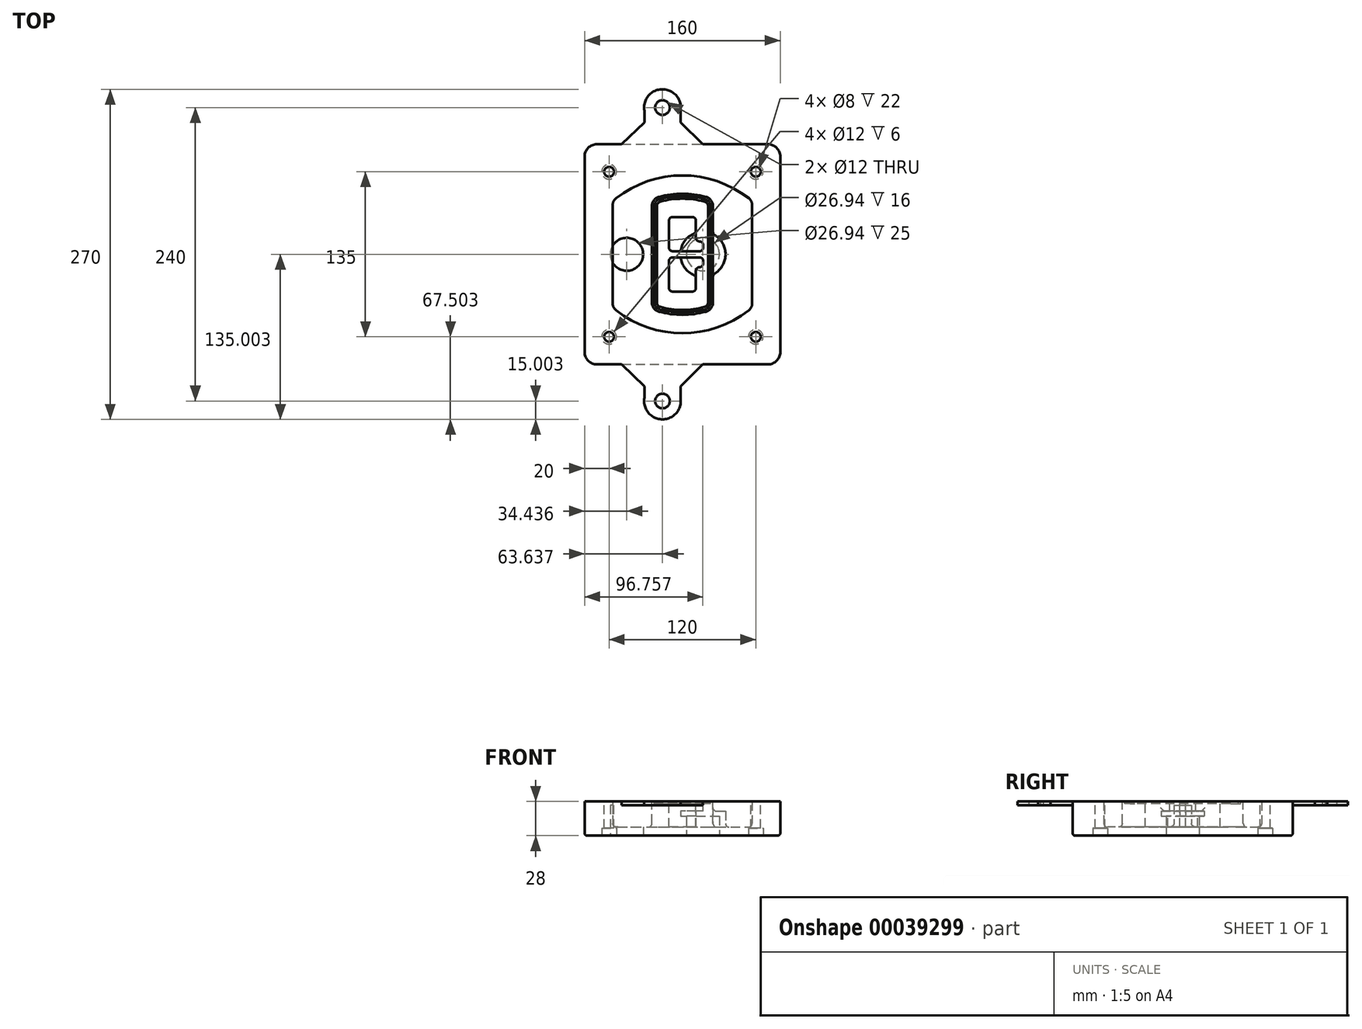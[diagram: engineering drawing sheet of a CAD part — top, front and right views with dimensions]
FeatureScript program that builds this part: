
annotation { "Feature Type Name" : "Feature", "Feature Type Description" : "" }
export const myFeature = defineFeature(function(context is Context, id is Id, definition is map)
    precondition{}
    {
        {
            var Q0;
            Q0=qCreatedBy(makeId("Top.planeOp"),FACE);
            var sketch = newSketch(context, id + "F0", { "sketchPlane" : qUnion([Q0])});
            skPoint(sketch, "E0.rect.middle", {"position": v(0, 0) * mm});
            skLineSegment(sketch, "E1.bottom", {"start": v(24.05, 28.38) * mm, "end": v(164.05, 28.38) * mm});
            skLineSegment(sketch, "E1.top", {"start": v(24.05, 208.38) * mm, "end": v(164.05, 208.38) * mm});
            skLineSegment(sketch, "E1.left", {"start": v(14.05, 38.38) * mm, "end": v(14.05, 198.38) * mm});
            skLineSegment(sketch, "E1.right", {"start": v(174.05, 38.38) * mm, "end": v(174.05, 198.38) * mm});
            skLineSegment(sketch, "E2", {"start": v(14.05, 208.38) * mm, "end": v(174.05, 28.38) * mm, "construction": true});
            skLineSegment(sketch, "E3", {"start": v(174.05, 208.38) * mm, "end": v(14.05, 28.38) * mm, "construction": true});
            skCircle(sketch, "E4", {"center": v(34.05, 185.88) * mm, "radius": 4 * mm});
            skCircle(sketch, "E5", {"center": v(154.05, 185.88) * mm, "radius": 4 * mm});
            skCircle(sketch, "E6", {"center": v(154.05, 50.88) * mm, "radius": 4 * mm});
            skCircle(sketch, "E7", {"center": v(34.05, 50.88) * mm, "radius": 4 * mm});
            skLineSegment(sketch, "E8", {"start": v(34.05, 185.88) * mm, "end": v(154.05, 185.88) * mm, "construction": true});
            skLineSegment(sketch, "E9", {"start": v(154.05, 185.88) * mm, "end": v(154.05, 50.88) * mm, "construction": true});
            skLineSegment(sketch, "E10", {"start": v(154.05, 50.88) * mm, "end": v(34.05, 50.88) * mm, "construction": true});
            skLineSegment(sketch, "E11", {"start": v(34.05, 50.88) * mm, "end": v(34.05, 185.88) * mm, "construction": true});
            skLineSegment(sketch, "E12", {"start": v(34.05, 158.68) * mm, "end": v(34.05, 78.09) * mm});
            skLineSegment(sketch, "E13", {"start": v(154.05, 158.68) * mm, "end": v(154.05, 78.09) * mm});
            skArc(sketch, "E14", {"start": v(150.2, 166.56) * mm, "mid": v(94.05, 185.88) * mm, "end": v(37.9, 166.56) * mm});
            skArc(sketch, "E15", {"start": v(37.9, 70.2) * mm, "mid": v(94.05, 50.88) * mm, "end": v(150.2, 70.2) * mm});
            skLineSegment(sketch, "E16", {"start": v(34.05, 118.38) * mm, "end": v(154.05, 118.38) * mm, "construction": true});
            skPoint(sketch, "E17.visualSharp", {"position": v(34.05, 73.38) * mm});
            skArc(sketch, "E17.filletArc", {"start": v(34.05, 78.09) * mm, "mid": v(35.06, 73.7) * mm, "end": v(37.9, 70.2) * mm});
            skPoint(sketch, "E18.visualSharp", {"position": v(34.05, 163.38) * mm});
            skArc(sketch, "E18.filletArc", {"start": v(37.9, 166.56) * mm, "mid": v(35.06, 163.06) * mm, "end": v(34.05, 158.68) * mm});
            skPoint(sketch, "E19.visualSharp", {"position": v(154.05, 163.38) * mm});
            skArc(sketch, "E19.filletArc", {"start": v(154.05, 158.68) * mm, "mid": v(153.04, 163.06) * mm, "end": v(150.2, 166.56) * mm});
            skPoint(sketch, "E20.visualSharp", {"position": v(154.05, 73.38) * mm});
            skArc(sketch, "E20.filletArc", {"start": v(150.2, 70.2) * mm, "mid": v(153.04, 73.7) * mm, "end": v(154.05, 78.09) * mm});
            skPoint(sketch, "E21.visualSharp", {"position": v(14.05, 208.38) * mm});
            skArc(sketch, "E21.filletArc", {"start": v(24.05, 208.38) * mm, "mid": v(16.98, 205.45) * mm, "end": v(14.05, 198.38) * mm});
            skPoint(sketch, "E22.visualSharp", {"position": v(174.05, 208.38) * mm});
            skArc(sketch, "E22.filletArc", {"start": v(174.05, 198.38) * mm, "mid": v(171.12, 205.45) * mm, "end": v(164.05, 208.38) * mm});
            skPoint(sketch, "E23.visualSharp", {"position": v(174.05, 28.38) * mm});
            skArc(sketch, "E23.filletArc", {"start": v(164.05, 28.38) * mm, "mid": v(171.12, 31.31) * mm, "end": v(174.05, 38.38) * mm});
            skPoint(sketch, "E24.visualSharp", {"position": v(14.05, 28.38) * mm});
            skArc(sketch, "E24.filletArc", {"start": v(14.05, 38.38) * mm, "mid": v(16.98, 31.31) * mm, "end": v(24.05, 28.38) * mm});
            skArc(sketch, "E25.0", {"start": v(151.05, 158.68) * mm, "mid": v(150.34, 161.75) * mm, "end": v(148.36, 164.2) * mm});
            skLineSegment(sketch, "E25.1", {"start": v(151.05, 158.68) * mm, "end": v(151.05, 78.09) * mm});
            skArc(sketch, "E25.2", {"start": v(148.36, 72.57) * mm, "mid": v(150.34, 75.02) * mm, "end": v(151.05, 78.09) * mm});
            skArc(sketch, "E25.3", {"start": v(39.74, 72.57) * mm, "mid": v(94.05, 53.88) * mm, "end": v(148.36, 72.57) * mm});
            skArc(sketch, "E25.4", {"start": v(37.05, 78.09) * mm, "mid": v(37.76, 75.02) * mm, "end": v(39.74, 72.57) * mm});
            skArc(sketch, "E25.5", {"start": v(148.36, 164.2) * mm, "mid": v(94.05, 182.88) * mm, "end": v(39.74, 164.2) * mm});
            skLineSegment(sketch, "E25.6", {"start": v(37.05, 158.68) * mm, "end": v(37.05, 78.09) * mm});
            skArc(sketch, "E25.7", {"start": v(39.74, 164.2) * mm, "mid": v(37.76, 161.75) * mm, "end": v(37.05, 158.68) * mm});
            skArc(sketch, "E26.0", {"start": v(35.43, 169.71) * mm, "mid": v(31.47, 164.82) * mm, "end": v(30.05, 158.68) * mm});
            skArc(sketch, "E26.1", {"start": v(152.67, 169.71) * mm, "mid": v(94.05, 189.88) * mm, "end": v(35.43, 169.71) * mm});
            skArc(sketch, "E26.2", {"start": v(158.05, 158.68) * mm, "mid": v(156.63, 164.82) * mm, "end": v(152.67, 169.71) * mm});
            skLineSegment(sketch, "E26.3", {"start": v(158.05, 158.68) * mm, "end": v(158.05, 78.09) * mm});
            skArc(sketch, "E26.4", {"start": v(152.67, 67.05) * mm, "mid": v(156.63, 71.95) * mm, "end": v(158.05, 78.09) * mm});
            skLineSegment(sketch, "E26.5", {"start": v(30.05, 158.68) * mm, "end": v(30.05, 78.09) * mm});
            skArc(sketch, "E26.6", {"start": v(35.43, 67.05) * mm, "mid": v(94.05, 46.88) * mm, "end": v(152.67, 67.05) * mm});
            skArc(sketch, "E26.7", {"start": v(30.05, 78.09) * mm, "mid": v(31.47, 71.95) * mm, "end": v(35.43, 67.05) * mm});
            skSolve(sketch);
        }
        {
            var Q0;
            Q0=makeQuery(id+"F0.imprint","IMPRINT",FACE,{"disambiguationData":[TD([[makeQuery(id+"F0.imprint","IMPRINT",EDGE,{"derivedFrom":sQuery(id+"F0.wireOp",EDGE,"E1.bottom")}),1.0]])]});
            var Q1;
            Q1=makeQuery(id+"F0.imprint","IMPRINT",FACE,{"disambiguationData":[TD([[makeQuery(id+"F0.imprint","IMPRINT",EDGE,{"derivedFrom":sQuery(id+"F0.wireOp",EDGE,"E12")}),1.0]])]});
            var Q2;
            Q2=makeQuery(id+"F0.imprint","IMPRINT",FACE,{"disambiguationData":[TD([[makeQuery(id+"F0.imprint","IMPRINT",EDGE,{"derivedFrom":sQuery(id+"F0.wireOp",EDGE,"E25.0")}),1.0]])]});
            var Q3;
            Q3=makeQuery(id+"F0.imprint","IMPRINT",FACE,{"disambiguationData":[TD([[makeQuery(id+"F0.imprint","IMPRINT",EDGE,{"derivedFrom":sQuery(id+"F0.wireOp",EDGE,"E12")}),-1.0]])]});
            extrude(context, id + "F1", {"entities" : qUnion([Q0, Q1, Q2, Q3]), "oppositeDirection" : true, "depth" : 25 * mm});
        }
        {
            var Q0;
            Q0=makeQuery(id+"F0.imprint","IMPRINT",FACE,{"disambiguationData":[TD([[makeQuery(id+"F0.imprint","IMPRINT",EDGE,{"derivedFrom":sQuery(id+"F0.wireOp",EDGE,"E12")}),1.0]])]});
            extrude(context, id + "F2", {"entities" : qUnion([Q0]), "operationType" : NewBodyOperationType.ADD, "depth" : 3 * mm});
        }
        {
            var Q0;
            Q0=makeQuery(id+"F0.imprint","IMPRINT",FACE,{"disambiguationData":[TD([[makeQuery(id+"F0.imprint","IMPRINT",EDGE,{"derivedFrom":sQuery(id+"F0.wireOp",EDGE,"E25.0")}),1.0]])]});
            extrude(context, id + "F3", {"entities" : qUnion([Q0]), "operationType" : NewBodyOperationType.REMOVE, "oppositeDirection" : true, "depth" : 18 * mm});
        }
        {
            var Q0;
            Q0=makeQuery(id+"F2.opExtrude","CAP_FACE",FACE,{"disambiguationData":[OSD([sQuery(id+"F0.wireOp",EDGE,"E12"),sQuery(id+"F0.wireOp",EDGE,"E13"),sQuery(id+"F0.wireOp",EDGE,"E14"),sQuery(id+"F0.wireOp",EDGE,"E15"),sQuery(id+"F0.wireOp",EDGE,"E17.filletArc"),sQuery(id+"F0.wireOp",EDGE,"E18.filletArc"),sQuery(id+"F0.wireOp",EDGE,"E19.filletArc"),sQuery(id+"F0.wireOp",EDGE,"E20.filletArc"),sQuery(id+"F0.wireOp",EDGE,"E25.0"),sQuery(id+"F0.wireOp",EDGE,"E25.1"),sQuery(id+"F0.wireOp",EDGE,"E25.2"),sQuery(id+"F0.wireOp",EDGE,"E25.3"),sQuery(id+"F0.wireOp",EDGE,"E25.4"),sQuery(id+"F0.wireOp",EDGE,"E25.5"),sQuery(id+"F0.wireOp",EDGE,"E25.6"),sQuery(id+"F0.wireOp",EDGE,"E25.7")])],"isStart":false});
            var sketch = newSketch(context, id + "F4", { "sketchPlane" : qUnion([Q0])});
            skArc(sketch, "E27.0", {"start": v(74.97, 71.41) * mm, "mid": v(94.05, 68.88) * mm, "end": v(113.13, 71.41) * mm});
            skArc(sketch, "E28.0", {"start": v(113.13, 165.35) * mm, "mid": v(94.05, 167.88) * mm, "end": v(74.97, 165.35) * mm});
            skLineSegment(sketch, "E29", {"start": v(69.05, 157.63) * mm, "end": v(69.05, 79.14) * mm});
            skLineSegment(sketch, "E30", {"start": v(119.05, 157.63) * mm, "end": v(119.05, 79.14) * mm});
            skLineSegment(sketch, "E31", {"start": v(69.05, 163.48) * mm, "end": v(119.05, 163.48) * mm, "construction": true});
            skLineSegment(sketch, "E32", {"start": v(69.05, 73.28) * mm, "end": v(119.05, 73.28) * mm, "construction": true});
            skPoint(sketch, "E33.visualSharp", {"position": v(69.05, 163.48) * mm});
            skArc(sketch, "E33.filletArc", {"start": v(74.97, 165.35) * mm, "mid": v(70.7, 162.5) * mm, "end": v(69.05, 157.63) * mm});
            skPoint(sketch, "E34.visualSharp", {"position": v(119.05, 163.48) * mm});
            skArc(sketch, "E34.filletArc", {"start": v(119.05, 157.63) * mm, "mid": v(117.4, 162.5) * mm, "end": v(113.13, 165.35) * mm});
            skPoint(sketch, "E35.visualSharp", {"position": v(119.05, 73.28) * mm});
            skArc(sketch, "E35.filletArc", {"start": v(113.13, 71.41) * mm, "mid": v(117.4, 74.27) * mm, "end": v(119.05, 79.14) * mm});
            skPoint(sketch, "E36.visualSharp", {"position": v(69.05, 73.28) * mm});
            skArc(sketch, "E36.filletArc", {"start": v(69.05, 79.14) * mm, "mid": v(70.7, 74.27) * mm, "end": v(74.97, 71.41) * mm});
            skArc(sketch, "E37.0", {"start": v(148.36, 164.2) * mm, "mid": v(94.05, 182.88) * mm, "end": v(39.74, 164.2) * mm});
            skArc(sketch, "E37.1", {"start": v(39.74, 164.2) * mm, "mid": v(37.76, 161.75) * mm, "end": v(37.05, 158.68) * mm});
            skLineSegment(sketch, "E37.2", {"start": v(37.05, 158.68) * mm, "end": v(37.05, 78.09) * mm});
            skArc(sketch, "E37.3", {"start": v(37.05, 78.09) * mm, "mid": v(37.76, 75.02) * mm, "end": v(39.74, 72.57) * mm});
            skArc(sketch, "E37.4", {"start": v(39.74, 72.57) * mm, "mid": v(94.05, 53.88) * mm, "end": v(148.36, 72.57) * mm});
            skArc(sketch, "E37.5", {"start": v(148.36, 72.57) * mm, "mid": v(150.34, 75.02) * mm, "end": v(151.05, 78.09) * mm});
            skLineSegment(sketch, "E37.6", {"start": v(151.05, 158.68) * mm, "end": v(151.05, 78.09) * mm});
            skArc(sketch, "E37.7", {"start": v(151.05, 158.68) * mm, "mid": v(150.34, 161.75) * mm, "end": v(148.36, 164.2) * mm});
            skLineSegment(sketch, "E38.0", {"start": v(117.05, 157.63) * mm, "end": v(117.05, 79.14) * mm});
            skArc(sketch, "E38.1", {"start": v(112.61, 73.34) * mm, "mid": v(115.81, 75.49) * mm, "end": v(117.05, 79.14) * mm});
            skArc(sketch, "E38.2", {"start": v(75.49, 73.34) * mm, "mid": v(94.05, 70.88) * mm, "end": v(112.61, 73.34) * mm});
            skArc(sketch, "E38.3", {"start": v(71.05, 79.14) * mm, "mid": v(72.29, 75.49) * mm, "end": v(75.49, 73.34) * mm});
            skLineSegment(sketch, "E38.4", {"start": v(71.05, 157.63) * mm, "end": v(71.05, 79.14) * mm});
            skArc(sketch, "E38.5", {"start": v(117.05, 157.63) * mm, "mid": v(115.81, 161.28) * mm, "end": v(112.61, 163.42) * mm});
            skArc(sketch, "E38.6", {"start": v(75.49, 163.42) * mm, "mid": v(72.29, 161.28) * mm, "end": v(71.05, 157.63) * mm});
            skArc(sketch, "E38.7", {"start": v(112.61, 163.42) * mm, "mid": v(94.05, 165.88) * mm, "end": v(75.49, 163.42) * mm});
            skArc(sketch, "E39.0", {"start": v(115.05, 157.63) * mm, "mid": v(114.23, 160.06) * mm, "end": v(112.1, 161.5) * mm});
            skLineSegment(sketch, "E39.1", {"start": v(115.05, 157.63) * mm, "end": v(115.05, 79.14) * mm});
            skArc(sketch, "E39.2", {"start": v(112.1, 75.27) * mm, "mid": v(114.23, 76.7) * mm, "end": v(115.05, 79.14) * mm});
            skArc(sketch, "E39.3", {"start": v(76, 75.27) * mm, "mid": v(94.05, 72.88) * mm, "end": v(112.1, 75.27) * mm});
            skArc(sketch, "E39.4", {"start": v(73.05, 79.14) * mm, "mid": v(73.87, 76.7) * mm, "end": v(76, 75.27) * mm});
            skArc(sketch, "E39.5", {"start": v(112.1, 161.5) * mm, "mid": v(94.05, 163.88) * mm, "end": v(76, 161.5) * mm});
            skLineSegment(sketch, "E39.6", {"start": v(73.05, 157.63) * mm, "end": v(73.05, 79.14) * mm});
            skArc(sketch, "E39.7", {"start": v(76, 161.5) * mm, "mid": v(73.87, 160.06) * mm, "end": v(73.05, 157.63) * mm});
            skLineSegment(sketch, "E40", {"start": v(69.05, 118.38) * mm, "end": v(119.05, 118.38) * mm, "construction": true});
            skLineSegment(sketch, "E41", {"start": v(83.05, 123.88) * mm, "end": v(83.05, 145.88) * mm});
            skLineSegment(sketch, "E42", {"start": v(86.05, 148.88) * mm, "end": v(102.05, 148.88) * mm});
            skLineSegment(sketch, "E43", {"start": v(105.05, 145.88) * mm, "end": v(105.05, 131.88) * mm});
            skLineSegment(sketch, "E44", {"start": v(108.05, 128.88) * mm, "end": v(108.05, 128.88) * mm});
            skLineSegment(sketch, "E45", {"start": v(111.05, 125.88) * mm, "end": v(111.05, 123.88) * mm});
            skLineSegment(sketch, "E46", {"start": v(108.05, 120.88) * mm, "end": v(86.05, 120.88) * mm});
            skPoint(sketch, "E47.visualSharp", {"position": v(83.05, 148.88) * mm});
            skArc(sketch, "E47.filletArc", {"start": v(86.05, 148.88) * mm, "mid": v(83.93, 148) * mm, "end": v(83.05, 145.88) * mm});
            skPoint(sketch, "E48.visualSharp", {"position": v(105.05, 148.88) * mm});
            skArc(sketch, "E48.filletArc", {"start": v(105.05, 145.88) * mm, "mid": v(104.17, 148) * mm, "end": v(102.05, 148.88) * mm});
            skPoint(sketch, "E49.visualSharp", {"position": v(105.05, 128.88) * mm});
            skArc(sketch, "E49.filletArc", {"start": v(105.05, 131.88) * mm, "mid": v(105.93, 129.76) * mm, "end": v(108.05, 128.88) * mm});
            skPoint(sketch, "E50.visualSharp", {"position": v(111.05, 128.88) * mm});
            skArc(sketch, "E50.filletArc", {"start": v(111.05, 125.88) * mm, "mid": v(110.17, 128) * mm, "end": v(108.05, 128.88) * mm});
            skPoint(sketch, "E51.visualSharp", {"position": v(111.05, 120.88) * mm});
            skArc(sketch, "E51.filletArc", {"start": v(108.05, 120.88) * mm, "mid": v(110.17, 121.76) * mm, "end": v(111.05, 123.88) * mm});
            skPoint(sketch, "E52.visualSharp", {"position": v(83.05, 120.88) * mm});
            skArc(sketch, "E52.filletArc", {"start": v(83.05, 123.88) * mm, "mid": v(83.93, 121.76) * mm, "end": v(86.05, 120.88) * mm});
            skLineSegment(sketch, "E53.0.MirrorCS", {"start": v(108.05, 115.88) * mm, "end": v(86.05, 115.88) * mm});
            skArc(sketch, "E54.0.MirrorCS", {"start": v(83.05, 112.88) * mm, "mid": v(83.93, 115) * mm, "end": v(86.05, 115.88) * mm});
            skLineSegment(sketch, "E55.0.MirrorCS", {"start": v(83.05, 112.88) * mm, "end": v(83.05, 90.88) * mm});
            skArc(sketch, "E56.0.MirrorCS", {"start": v(86.05, 87.88) * mm, "mid": v(83.93, 88.76) * mm, "end": v(83.05, 90.88) * mm});
            skLineSegment(sketch, "E57.0.MirrorCS", {"start": v(86.05, 87.88) * mm, "end": v(102.05, 87.88) * mm});
            skArc(sketch, "E58.0.MirrorCS", {"start": v(105.05, 90.88) * mm, "mid": v(104.17, 88.76) * mm, "end": v(102.05, 87.88) * mm});
            skLineSegment(sketch, "E59.0.MirrorCS", {"start": v(105.05, 90.88) * mm, "end": v(105.05, 104.88) * mm});
            skArc(sketch, "E60.0.MirrorCS", {"start": v(105.05, 104.88) * mm, "mid": v(105.93, 107) * mm, "end": v(108.05, 107.88) * mm});
            skArc(sketch, "E61.0.MirrorCS", {"start": v(111.05, 110.88) * mm, "mid": v(110.17, 108.76) * mm, "end": v(108.05, 107.88) * mm});
            skLineSegment(sketch, "E62.0.MirrorCS", {"start": v(111.05, 110.88) * mm, "end": v(111.05, 112.88) * mm});
            skArc(sketch, "E63.0.MirrorCS", {"start": v(108.05, 115.88) * mm, "mid": v(110.17, 115) * mm, "end": v(111.05, 112.88) * mm});
            skSolve(sketch);
        }
        {
            var Q0;
            Q0=makeQuery(id+"F4.imprint","IMPRINT",FACE,{"disambiguationData":[TD([[makeQuery(id+"F4.imprint","IMPRINT",EDGE,{"derivedFrom":sQuery(id+"F4.wireOp",EDGE,"E27.0")}),1.0]])]});
            var Q1;
            Q1=makeQuery(id+"F4.imprint","IMPRINT",FACE,{"disambiguationData":[TD([[makeQuery(id+"F4.imprint","IMPRINT",EDGE,{"derivedFrom":sQuery(id+"F4.wireOp",EDGE,"E38.0")}),-1.0]])]});
            var Q2;
            Q2=makeQuery(id+"F4.imprint","IMPRINT",FACE,{"disambiguationData":[TD([[makeQuery(id+"F4.imprint","IMPRINT",EDGE,{"derivedFrom":sQuery(id+"F4.wireOp",EDGE,"E39.0")}),1.0]])]});
            extrude(context, id + "F5", {"entities" : qUnion([Q0, Q1, Q2]), "operationType" : NewBodyOperationType.ADD, "endBound" : BoundingType.UP_TO_NEXT, "oppositeDirection" : true, "depth" : 25 * mm});
        }
        {
            var Q0;
            Q0=makeQuery(id+"F4.imprint","IMPRINT",FACE,{"disambiguationData":[TD([[makeQuery(id+"F4.imprint","IMPRINT",EDGE,{"derivedFrom":sQuery(id+"F4.wireOp",EDGE,"E38.0")}),-1.0]])]});
            extrude(context, id + "F6", {"entities" : qUnion([Q0]), "operationType" : NewBodyOperationType.REMOVE, "oppositeDirection" : true, "depth" : 2 * mm});
        }
        {
            var Q0;
            Q0=makeQuery(id+"F1.opExtrude","CAP_FACE",FACE,{"disambiguationData":[OSD([sQuery(id+"F0.wireOp",EDGE,"E1.bottom"),sQuery(id+"F0.wireOp",EDGE,"E1.top"),sQuery(id+"F0.wireOp",EDGE,"E1.left"),sQuery(id+"F0.wireOp",EDGE,"E1.right"),sQuery(id+"F0.wireOp",EDGE,"E4"),sQuery(id+"F0.wireOp",EDGE,"E5"),sQuery(id+"F0.wireOp",EDGE,"E6"),sQuery(id+"F0.wireOp",EDGE,"E7"),sQuery(id+"F0.wireOp",EDGE,"E21.filletArc"),sQuery(id+"F0.wireOp",EDGE,"E22.filletArc"),sQuery(id+"F0.wireOp",EDGE,"E23.filletArc"),sQuery(id+"F0.wireOp",EDGE,"E24.filletArc")])],"isStart":false});
            var sketch = newSketch(context, id + "F7", { "sketchPlane" : qUnion([Q0])});
            skCircle(sketch, "E64", {"center": v(110.8, -118.38) * mm, "radius": 13.47 * mm});
            skCircle(sketch, "E65", {"center": v(48.49, -118.38) * mm, "radius": 13.47 * mm});
            skLineSegment(sketch, "E66", {"start": v(174.05, -118.38) * mm, "end": v(14.05, -118.38) * mm});
            skCircle(sketch, "E67", {"center": v(110.8, -118.38) * mm, "radius": 18.47 * mm});
            skCircle(sketch, "E68", {"center": v(154.05, -185.88) * mm, "radius": 6 * mm});
            skCircle(sketch, "E69", {"center": v(34.05, -185.88) * mm, "radius": 6 * mm});
            skCircle(sketch, "E70", {"center": v(34.05, -50.88) * mm, "radius": 6 * mm});
            skCircle(sketch, "E71", {"center": v(154.05, -50.88) * mm, "radius": 6 * mm});
            skSolve(sketch);
        }
        {
            var Q0;
            {var subQ1=sQuery(id+"F7.wireOp",EDGE,"E66");var subQ4=sQuery(id+"F7.wireOp",EDGE,"E64");var subQ6=makeQuery(id+"F7.imprint","INTERSECT",VERTEX,{"disambiguationData":[OD(0.0)],"derivedFrom":[subQ4,subQ1]});Q0=makeQuery(id+"F7.imprint","IMPRINT",FACE,{"disambiguationData":[TD([[makeQuery(id+"F7.imprint","IMPRINT",EDGE,{"disambiguationData":[TD([[subQ6,-1.0]])],"derivedFrom":subQ4}),-1.0]])]});}
            var Q1;
            {var subQ0=sQuery(id+"F7.wireOp",EDGE,"E66");var subQ1=sQuery(id+"F7.wireOp",EDGE,"E64");var subQ3=makeQuery(id+"F7.imprint","INTERSECT",VERTEX,{"disambiguationData":[OD(0.0)],"derivedFrom":[subQ1,subQ0]});Q1=makeQuery(id+"F7.imprint","IMPRINT",FACE,{"disambiguationData":[TD([[makeQuery(id+"F7.imprint","IMPRINT",EDGE,{"disambiguationData":[TD([[subQ3,-1.0]])],"derivedFrom":subQ1}),1.0]])]});}
            var Q2;
            {var subQ0=sQuery(id+"F7.wireOp",EDGE,"E66");var subQ1=sQuery(id+"F7.wireOp",EDGE,"E64");var subQ3=makeQuery(id+"F7.imprint","INTERSECT",VERTEX,{"disambiguationData":[OD(0.0)],"derivedFrom":[subQ1,subQ0]});Q2=makeQuery(id+"F7.imprint","IMPRINT",FACE,{"disambiguationData":[TD([[makeQuery(id+"F7.imprint","IMPRINT",EDGE,{"disambiguationData":[TD([[subQ3,1.0]])],"derivedFrom":subQ1}),1.0]])]});}
            var Q3;
            {var subQ1=sQuery(id+"F7.wireOp",EDGE,"E66");var subQ4=sQuery(id+"F7.wireOp",EDGE,"E64");var subQ6=makeQuery(id+"F7.imprint","INTERSECT",VERTEX,{"disambiguationData":[OD(0.0)],"derivedFrom":[subQ4,subQ1]});Q3=makeQuery(id+"F7.imprint","IMPRINT",FACE,{"disambiguationData":[TD([[makeQuery(id+"F7.imprint","IMPRINT",EDGE,{"disambiguationData":[TD([[subQ6,1.0]])],"derivedFrom":subQ4}),-1.0]])]});}
            extrude(context, id + "F8", {"entities" : qUnion([Q0, Q1, Q2, Q3]), "operationType" : NewBodyOperationType.ADD, "oppositeDirection" : true, "depth" : 20 * mm});
        }
        {
            var Q0;
            {var subQ0=sQuery(id+"F7.wireOp",EDGE,"E66");var subQ1=sQuery(id+"F7.wireOp",EDGE,"E64");var subQ3=makeQuery(id+"F7.imprint","INTERSECT",VERTEX,{"disambiguationData":[OD(0.0)],"derivedFrom":[subQ1,subQ0]});Q0=makeQuery(id+"F7.imprint","IMPRINT",FACE,{"disambiguationData":[TD([[makeQuery(id+"F7.imprint","IMPRINT",EDGE,{"disambiguationData":[TD([[subQ3,-1.0]])],"derivedFrom":subQ1}),1.0]])]});}
            var Q1;
            {var subQ0=sQuery(id+"F7.wireOp",EDGE,"E66");var subQ1=sQuery(id+"F7.wireOp",EDGE,"E64");var subQ3=makeQuery(id+"F7.imprint","INTERSECT",VERTEX,{"disambiguationData":[OD(0.0)],"derivedFrom":[subQ1,subQ0]});Q1=makeQuery(id+"F7.imprint","IMPRINT",FACE,{"disambiguationData":[TD([[makeQuery(id+"F7.imprint","IMPRINT",EDGE,{"disambiguationData":[TD([[subQ3,1.0]])],"derivedFrom":subQ1}),1.0]])]});}
            extrude(context, id + "F9", {"entities" : qUnion([Q0, Q1]), "operationType" : NewBodyOperationType.REMOVE, "oppositeDirection" : true, "depth" : 16 * mm});
        }
        {
            var Q0;
            {var subQ0=sQuery(id+"F7.wireOp",EDGE,"E66");var subQ1=sQuery(id+"F7.wireOp",EDGE,"E65");var subQ3=makeQuery(id+"F7.imprint","INTERSECT",VERTEX,{"disambiguationData":[OD(0.0)],"derivedFrom":[subQ1,subQ0]});Q0=makeQuery(id+"F7.imprint","IMPRINT",FACE,{"disambiguationData":[TD([[makeQuery(id+"F7.imprint","IMPRINT",EDGE,{"disambiguationData":[TD([[subQ3,-1.0]])],"derivedFrom":subQ1}),1.0]])]});}
            var Q1;
            {var subQ0=sQuery(id+"F7.wireOp",EDGE,"E66");var subQ1=sQuery(id+"F7.wireOp",EDGE,"E65");var subQ3=makeQuery(id+"F7.imprint","INTERSECT",VERTEX,{"disambiguationData":[OD(0.0)],"derivedFrom":[subQ1,subQ0]});Q1=makeQuery(id+"F7.imprint","IMPRINT",FACE,{"disambiguationData":[TD([[makeQuery(id+"F7.imprint","IMPRINT",EDGE,{"disambiguationData":[TD([[subQ3,1.0]])],"derivedFrom":subQ1}),1.0]])]});}
            extrude(context, id + "F10", {"entities" : qUnion([Q0, Q1]), "operationType" : NewBodyOperationType.REMOVE, "oppositeDirection" : true, "depth" : 25 * mm});
        }
        {
            var Q0;
            Q0=makeQuery(id+"F7.imprint","IMPRINT",FACE,{"disambiguationData":[TD([[makeQuery(id+"F7.imprint","IMPRINT",EDGE,{"derivedFrom":sQuery(id+"F7.wireOp",EDGE,"E68")}),1.0]])]});
            var Q1;
            Q1=makeQuery(id+"F7.imprint","IMPRINT",FACE,{"disambiguationData":[TD([[makeQuery(id+"F7.imprint","IMPRINT",EDGE,{"derivedFrom":makeQuery(id+"F1.opExtrude","CAP_EDGE",EDGE,{"disambiguationData":[OSD([sQuery(id+"F0.wireOp",EDGE,"E5")])],"isStart":false})}),-1.0]])]});
            var Q2;
            Q2=makeQuery(id+"F7.imprint","IMPRINT",FACE,{"disambiguationData":[TD([[makeQuery(id+"F7.imprint","IMPRINT",EDGE,{"derivedFrom":sQuery(id+"F7.wireOp",EDGE,"E69")}),1.0]])]});
            var Q3;
            Q3=makeQuery(id+"F7.imprint","IMPRINT",FACE,{"disambiguationData":[TD([[makeQuery(id+"F7.imprint","IMPRINT",EDGE,{"derivedFrom":makeQuery(id+"F1.opExtrude","CAP_EDGE",EDGE,{"disambiguationData":[OSD([sQuery(id+"F0.wireOp",EDGE,"E4")])],"isStart":false})}),-1.0]])]});
            var Q4;
            Q4=makeQuery(id+"F7.imprint","IMPRINT",FACE,{"disambiguationData":[TD([[makeQuery(id+"F7.imprint","IMPRINT",EDGE,{"derivedFrom":sQuery(id+"F7.wireOp",EDGE,"E70")}),1.0]])]});
            var Q5;
            Q5=makeQuery(id+"F7.imprint","IMPRINT",FACE,{"disambiguationData":[TD([[makeQuery(id+"F7.imprint","IMPRINT",EDGE,{"derivedFrom":makeQuery(id+"F1.opExtrude","CAP_EDGE",EDGE,{"disambiguationData":[OSD([sQuery(id+"F0.wireOp",EDGE,"E7")])],"isStart":false})}),-1.0]])]});
            var Q6;
            Q6=makeQuery(id+"F7.imprint","IMPRINT",FACE,{"disambiguationData":[TD([[makeQuery(id+"F7.imprint","IMPRINT",EDGE,{"derivedFrom":sQuery(id+"F7.wireOp",EDGE,"E71")}),1.0]])]});
            var Q7;
            Q7=makeQuery(id+"F7.imprint","IMPRINT",FACE,{"disambiguationData":[TD([[makeQuery(id+"F7.imprint","IMPRINT",EDGE,{"derivedFrom":makeQuery(id+"F1.opExtrude","CAP_EDGE",EDGE,{"disambiguationData":[OSD([sQuery(id+"F0.wireOp",EDGE,"E6")])],"isStart":false})}),-1.0]])]});
            extrude(context, id + "F11", {"entities" : qUnion([Q0, Q1, Q2, Q3, Q4, Q5, Q6, Q7]), "operationType" : NewBodyOperationType.REMOVE, "oppositeDirection" : true, "depth" : 6 * mm});
        }
        {
            var Q0;
            Q0=makeQuery(id+"F9.boolean.opBoolean","COPY",FACE,{"derivedFrom":makeQuery(id+"F9.opExtrude","CAP_FACE",FACE,{"disambiguationData":[OSD([sQuery(id+"F7.wireOp",EDGE,"E64")])],"isStart":false})});
            var sketch = newSketch(context, id + "F12", { "sketchPlane" : qUnion([Q0])});
            skArc(sketch, "E72.0", {"start": v(105.05, -100.83) * mm, "mid": v(96.62, -106.56) * mm, "end": v(92.5, -115.88) * mm});
            skArc(sketch, "E72.1", {"start": v(92.5, -120.88) * mm, "mid": v(96.62, -130.2) * mm, "end": v(105.05, -135.93) * mm});
            skLineSegment(sketch, "E73", {"start": v(92.5, -120.88) * mm, "end": v(108.05, -120.88) * mm});
            skLineSegment(sketch, "E74.0", {"start": v(108.05, -115.88) * mm, "end": v(92.5, -115.88) * mm});
            skArc(sketch, "E74.1", {"start": v(108.05, -115.88) * mm, "mid": v(110.17, -115) * mm, "end": v(111.05, -112.88) * mm});
            skLineSegment(sketch, "E74.2", {"start": v(111.05, -110.88) * mm, "end": v(111.05, -112.88) * mm});
            skArc(sketch, "E74.3", {"start": v(111.05, -110.88) * mm, "mid": v(110.17, -108.76) * mm, "end": v(108.05, -107.88) * mm});
            skArc(sketch, "E74.4", {"start": v(105.05, -104.88) * mm, "mid": v(105.93, -107) * mm, "end": v(108.05, -107.88) * mm});
            skLineSegment(sketch, "E74.5", {"start": v(105.05, -100.83) * mm, "end": v(105.05, -104.88) * mm});
            skLineSegment(sketch, "E74.7", {"start": v(108.05, -120.88) * mm, "end": v(92.5, -120.88) * mm});
            skArc(sketch, "E74.8", {"start": v(108.05, -120.88) * mm, "mid": v(110.17, -121.76) * mm, "end": v(111.05, -123.88) * mm});
            skLineSegment(sketch, "E74.9", {"start": v(111.05, -125.88) * mm, "end": v(111.05, -123.88) * mm});
            skArc(sketch, "E74.10", {"start": v(111.05, -125.88) * mm, "mid": v(110.17, -128) * mm, "end": v(108.05, -128.88) * mm});
            skArc(sketch, "E74.11", {"start": v(105.05, -131.88) * mm, "mid": v(105.93, -129.76) * mm, "end": v(108.05, -128.88) * mm});
            skLineSegment(sketch, "E74.12", {"start": v(105.05, -135.93) * mm, "end": v(105.05, -131.88) * mm});
            skPoint(sketch, "E75.orphan", {"position": v(105.05, -145.88) * mm});
            skPoint(sketch, "E76.orphan", {"position": v(86.05, -120.88) * mm});
            skPoint(sketch, "E77.orphan", {"position": v(86.05, -115.88) * mm});
            skPoint(sketch, "E78.orphan", {"position": v(105.05, -90.88) * mm});
            skSolve(sketch);
        }
        {
            var Q0;
            {var subQ7=sQuery(id+"F12.wireOp",EDGE,"E72.0");var subQ14=sQuery(id+"F12.wireOp",EDGE,"E72.1");var subQ16=sQuery(id+"F12.wireOp",EDGE,"E74.1");var subQ18=sQuery(id+"F12.wireOp",EDGE,"E74.8");Q0=qUnion([makeQuery(id+"F12.imprint","IMPRINT",FACE,{"disambiguationData":[TD([[makeQuery(id+"F12.imprint","IMPRINT",EDGE,{"derivedFrom":subQ7}),1.0]])]}),makeQuery(id+"F12.imprint","IMPRINT",FACE,{"disambiguationData":[TD([[makeQuery(id+"F12.imprint","IMPRINT",EDGE,{"derivedFrom":subQ14}),1.0]])]}),makeQuery(id+"F12.imprint","IMPRINT",FACE,{"disambiguationData":[TD([[makeQuery(id+"F12.imprint","IMPRINT",EDGE,{"derivedFrom":subQ16}),1.0]])]}),makeQuery(id+"F12.imprint","IMPRINT",FACE,{"disambiguationData":[TD([[makeQuery(id+"F12.imprint","IMPRINT",EDGE,{"derivedFrom":subQ18}),-1.0]])]})]);}
            var Q1;
            Q1=makeQuery(id+"F5.boolean.opBoolean","SPLIT",FACE,{"disambiguationData":[TD([makeQuery(id+"F5.opExtrude","SWEPT_FACE",FACE,{"disambiguationData":[OSD([sQuery(id+"F4.wireOp",EDGE,"E41")])]})])],"derivedFrom":makeQuery(id+"F3.boolean.opBoolean","COPY",FACE,{"derivedFrom":makeQuery(id+"F3.opExtrude","CAP_FACE",FACE,{"disambiguationData":[OSD([sQuery(id+"F0.wireOp",EDGE,"E25.0"),sQuery(id+"F0.wireOp",EDGE,"E25.1"),sQuery(id+"F0.wireOp",EDGE,"E25.2"),sQuery(id+"F0.wireOp",EDGE,"E25.3"),sQuery(id+"F0.wireOp",EDGE,"E25.4"),sQuery(id+"F0.wireOp",EDGE,"E25.5"),sQuery(id+"F0.wireOp",EDGE,"E25.6"),sQuery(id+"F0.wireOp",EDGE,"E25.7")])],"isStart":false})})});
            extrude(context, id + "F13", {"entities" : qUnion([Q0]), "operationType" : NewBodyOperationType.REMOVE, "endBound" : BoundingType.UP_TO_SURFACE, "endBoundEntityFace" : qUnion([Q1]), "depth" : 25 * mm});
        }
        {
            var Q0;
            Q0=makeQuery(id+"F3.boolean.opBoolean","COPY",EDGE,{"derivedFrom":makeQuery(id+"F3.opExtrude","CAP_EDGE",EDGE,{"disambiguationData":[OSD([sQuery(id+"F0.wireOp",EDGE,"E25.6")])],"isStart":false})});
            var Q1;
            Q1=makeQuery(id+"F8.boolean.opBoolean","INTERSECT",EDGE,{"derivedFrom":[makeQuery(id+"F5.opExtrude","SWEPT_FACE",FACE,{"disambiguationData":[OSD([sQuery(id+"F4.wireOp",EDGE,"E30")])]}),makeQuery(id+"F8.opExtrude","CAP_FACE",FACE,{"disambiguationData":[OSD([sQuery(id+"F7.wireOp",EDGE,"E67")])],"isStart":false})]});
            var Q2;
            Q2=makeQuery(id+"F8.boolean.opBoolean","INTERSECT",EDGE,{"disambiguationData":[OD(1.0)],"derivedFrom":[makeQuery(id+"F5.opExtrude","SWEPT_FACE",FACE,{"disambiguationData":[OSD([sQuery(id+"F4.wireOp",EDGE,"E30")])]}),makeQuery(id+"F8.opExtrude","SWEPT_FACE",FACE,{"disambiguationData":[OSD([sQuery(id+"F7.wireOp",EDGE,"E67")])]})]});
            var Q3;
            {var subQ0=sQuery(id+"F4.wireOp",EDGE,"E30");Q3=makeQuery(id+"F8.boolean.opBoolean","SPLIT",EDGE,{"disambiguationData":[TD([makeQuery(id+"F5.opExtrude","SWEPT_FACE",FACE,{"disambiguationData":[OSD([sQuery(id+"F4.wireOp",EDGE,"E35.filletArc")])]})])],"derivedFrom":makeQuery(id+"F5.opExtrude","CAP_EDGE",EDGE,{"disambiguationData":[OSD([subQ0])],"isStart":false})});}
            var Q4;
            {var subQ0=sQuery(id+"F0.wireOp",EDGE,"E25.7");var subQ1=sQuery(id+"F0.wireOp",EDGE,"E25.1");var subQ2=sQuery(id+"F0.wireOp",EDGE,"E25.6");var subQ3=sQuery(id+"F0.wireOp",EDGE,"E25.5");var subQ4=sQuery(id+"F0.wireOp",EDGE,"E25.4");var subQ5=sQuery(id+"F0.wireOp",EDGE,"E25.0");var subQ6=sQuery(id+"F0.wireOp",EDGE,"E25.2");var subQ7=sQuery(id+"F0.wireOp",EDGE,"E25.3");Q4=makeQuery(id+"F8.boolean.opBoolean","INTERSECT",EDGE,{"derivedFrom":[makeQuery(id+"F5.boolean.opBoolean","SPLIT",FACE,{"disambiguationData":[TD([makeQuery(id+"F2.opExtrude","SWEPT_FACE",FACE,{"disambiguationData":[OSD([subQ5])]})])],"derivedFrom":makeQuery(id+"F3.boolean.opBoolean","COPY",FACE,{"derivedFrom":makeQuery(id+"F3.opExtrude","CAP_FACE",FACE,{"disambiguationData":[OSD([subQ5,subQ1,subQ6,subQ7,subQ4,subQ3,subQ2,subQ0])],"isStart":false})})}),makeQuery(id+"F8.opExtrude","SWEPT_FACE",FACE,{"disambiguationData":[OSD([sQuery(id+"F7.wireOp",EDGE,"E67")])]})]});}
            var Q5;
            Q5=makeQuery(id+"F8.boolean.opBoolean","INTERSECT",EDGE,{"disambiguationData":[OD(0.0)],"derivedFrom":[makeQuery(id+"F5.opExtrude","SWEPT_FACE",FACE,{"disambiguationData":[OSD([sQuery(id+"F4.wireOp",EDGE,"E30")])]}),makeQuery(id+"F8.opExtrude","SWEPT_FACE",FACE,{"disambiguationData":[OSD([sQuery(id+"F7.wireOp",EDGE,"E67")])]})]});
            fillet(context, id + "F14", {"entities" : qUnion([Q0, Q1, Q2, Q3, Q4, Q5]), "radius" : 3 * mm, "tangentPropagation" : true, "allowEdgeOverflow" : false});
        }
        {
            var Q0;
            Q0=makeQuery(id+"F1.opExtrude","CAP_EDGE",EDGE,{"disambiguationData":[OSD([sQuery(id+"F0.wireOp",EDGE,"E1.bottom")])],"isStart":false});
            fillet(context, id + "F15", {"entities" : qUnion([Q0]), "radius" : 2 * mm, "tangentPropagation" : true, "allowEdgeOverflow" : false});
        }
        {
            var Q0;
            {var subQ0=sQuery(id+"F0.wireOp",EDGE,"E1.bottom");var subQ1=sQuery(id+"F0.wireOp",EDGE,"E1.top");var subQ2=sQuery(id+"F0.wireOp",EDGE,"E1.left");var subQ3=sQuery(id+"F0.wireOp",EDGE,"E1.right");var subQ4=sQuery(id+"F0.wireOp",EDGE,"E4");var subQ5=sQuery(id+"F0.wireOp",EDGE,"E5");var subQ6=sQuery(id+"F0.wireOp",EDGE,"E6");var subQ7=sQuery(id+"F0.wireOp",EDGE,"E7");var subQ8=sQuery(id+"F0.wireOp",EDGE,"E21.filletArc");var subQ9=sQuery(id+"F0.wireOp",EDGE,"E22.filletArc");var subQ10=sQuery(id+"F0.wireOp",EDGE,"E23.filletArc");var subQ11=sQuery(id+"F0.wireOp",EDGE,"E24.filletArc");Q0=makeQuery(id+"F2.boolean.opBoolean","SPLIT",FACE,{"disambiguationData":[TD([makeQuery(id+"F1.opExtrude","SWEPT_FACE",FACE,{"disambiguationData":[OSD([subQ0])]})])],"derivedFrom":makeQuery(id+"F1.opExtrude","CAP_FACE",FACE,{"disambiguationData":[OSD([subQ0,subQ1,subQ2,subQ3,subQ4,subQ5,subQ6,subQ7,subQ8,subQ9,subQ10,subQ11])],"isStart":true})});}
            var sketch = newSketch(context, id + "F16", { "sketchPlane" : qUnion([Q0])});
            skLineSegment(sketch, "E79", {"start": v(44.39, 208.38) * mm, "end": v(63.15, 226.38) * mm});
            skLineSegment(sketch, "E80", {"start": v(110.58, 208.38) * mm, "end": v(92.58, 226.38) * mm});
            skLineSegment(sketch, "E81", {"start": v(63.15, 226.38) * mm, "end": v(63.15, 234.69) * mm});
            skLineSegment(sketch, "E82", {"start": v(92.58, 226.38) * mm, "end": v(92.58, 236.62) * mm});
            skArc(sketch, "E83", {"start": v(92.58, 236.62) * mm, "mid": v(76.7, 253.35) * mm, "end": v(63.15, 234.69) * mm});
            skLineSegment(sketch, "E84", {"start": v(44.39, 208.38) * mm, "end": v(110.58, 208.38) * mm});
            skLineSegment(sketch, "E85", {"start": v(77.69, 238.38) * mm, "end": v(77.69, 208.38) * mm, "construction": true});
            skCircle(sketch, "E86", {"center": v(77.69, 238.38) * mm, "radius": 6 * mm});
            skLineSegment(sketch, "E87", {"start": v(14.05, 118.38) * mm, "end": v(174.05, 118.38) * mm, "construction": true});
            skLineSegment(sketch, "E88.MirrorCS", {"start": v(63.15, 10.38) * mm, "end": v(63.15, 2.08) * mm});
            skLineSegment(sketch, "E89.MirrorCS", {"start": v(110.58, 28.38) * mm, "end": v(92.58, 10.38) * mm});
            skLineSegment(sketch, "E90.MirrorCS", {"start": v(44.39, 28.38) * mm, "end": v(63.15, 10.38) * mm});
            skLineSegment(sketch, "E91.MirrorCS", {"start": v(77.69, -1.62) * mm, "end": v(77.69, 28.38) * mm, "construction": true});
            skLineSegment(sketch, "E92.MirrorCS", {"start": v(92.58, 10.38) * mm, "end": v(92.58, 0.15) * mm});
            skCircle(sketch, "E93.MirrorC", {"center": v(77.69, -1.62) * mm, "radius": 6 * mm});
            skArc(sketch, "E94.MirrorCS", {"start": v(92.58, 0.15) * mm, "mid": v(76.7, -16.59) * mm, "end": v(63.15, 2.08) * mm});
            skSolve(sketch);
        }
        {
            var Q0;
            Q0=makeQuery(id+"F16.imprint","IMPRINT",FACE,{"disambiguationData":[TD([[makeQuery(id+"F16.imprint","IMPRINT",EDGE,{"derivedFrom":sQuery(id+"F16.wireOp",EDGE,"E88.MirrorCS")}),1.0]])]});
            var Q1;
            Q1=makeQuery(id+"F16.imprint","IMPRINT",FACE,{"disambiguationData":[TD([[makeQuery(id+"F16.imprint","IMPRINT",EDGE,{"derivedFrom":sQuery(id+"F16.wireOp",EDGE,"E79")}),-1.0]])]});
            var Q2;
            {var subQ1=sQuery(id+"F16.wireOp",EDGE,"E84");Q2=makeQuery(id+"F16.imprint","IMPRINT",FACE,{"disambiguationData":[TD([[makeQuery(id+"F16.imprint","IMPRINT",EDGE,{"derivedFrom":subQ1}),-1.0]])]});}
            var Q3;
            {var subQ0=sQuery(id+"F4.wireOp",EDGE,"E63.0.MirrorCS");var subQ1=sQuery(id+"F4.wireOp",EDGE,"E62.0.MirrorCS");var subQ2=sQuery(id+"F4.wireOp",EDGE,"E61.0.MirrorCS");var subQ3=sQuery(id+"F4.wireOp",EDGE,"E60.0.MirrorCS");var subQ4=sQuery(id+"F4.wireOp",EDGE,"E59.0.MirrorCS");var subQ5=sQuery(id+"F4.wireOp",EDGE,"E58.0.MirrorCS");var subQ6=sQuery(id+"F4.wireOp",EDGE,"E57.0.MirrorCS");var subQ7=sQuery(id+"F4.wireOp",EDGE,"E56.0.MirrorCS");var subQ8=sQuery(id+"F4.wireOp",EDGE,"E55.0.MirrorCS");var subQ9=sQuery(id+"F4.wireOp",EDGE,"E54.0.MirrorCS");var subQ10=sQuery(id+"F4.wireOp",EDGE,"E53.0.MirrorCS");var subQ11=sQuery(id+"F4.wireOp",EDGE,"E52.filletArc");var subQ12=sQuery(id+"F4.wireOp",EDGE,"E45");var subQ13=sQuery(id+"F4.wireOp",EDGE,"E43");var subQ14=sQuery(id+"F4.wireOp",EDGE,"E42");var subQ15=sQuery(id+"F4.wireOp",EDGE,"E41");var subQ16=sQuery(id+"F4.wireOp",EDGE,"E46");var subQ17=sQuery(id+"F4.wireOp",EDGE,"E47.filletArc");var subQ18=sQuery(id+"F4.wireOp",EDGE,"E48.filletArc");var subQ19=sQuery(id+"F4.wireOp",EDGE,"E49.filletArc");var subQ20=sQuery(id+"F4.wireOp",EDGE,"E50.filletArc");var subQ21=sQuery(id+"F4.wireOp",EDGE,"E51.filletArc");Q3=makeQuery(id+"F6.boolean.opBoolean","SPLIT",FACE,{"disambiguationData":[TD([makeQuery(id+"F5.opExtrude","SWEPT_FACE",FACE,{"disambiguationData":[OSD([subQ15])]})])],"derivedFrom":makeQuery(id+"F5.opExtrude","CAP_FACE",FACE,{"disambiguationData":[OSD([sQuery(id+"F4.wireOp",EDGE,"E27.0"),sQuery(id+"F4.wireOp",EDGE,"E28.0"),sQuery(id+"F4.wireOp",EDGE,"E29"),sQuery(id+"F4.wireOp",EDGE,"E30"),sQuery(id+"F4.wireOp",EDGE,"E33.filletArc"),sQuery(id+"F4.wireOp",EDGE,"E34.filletArc"),sQuery(id+"F4.wireOp",EDGE,"E35.filletArc"),sQuery(id+"F4.wireOp",EDGE,"E36.filletArc"),subQ15,subQ14,subQ13,subQ12,subQ16,subQ17,subQ18,subQ19,subQ20,subQ21,subQ11,subQ10,subQ9,subQ8,subQ7,subQ6,subQ5,subQ4,subQ3,subQ2,subQ1,subQ0])],"isStart":true})});}
            extrude(context, id + "F17", {"entities" : qUnion([Q0, Q1, Q2]), "operationType" : NewBodyOperationType.ADD, "endBound" : BoundingType.UP_TO_SURFACE, "endBoundEntityFace" : qUnion([Q3]), "depth" : 25 * mm});
        }
    });
